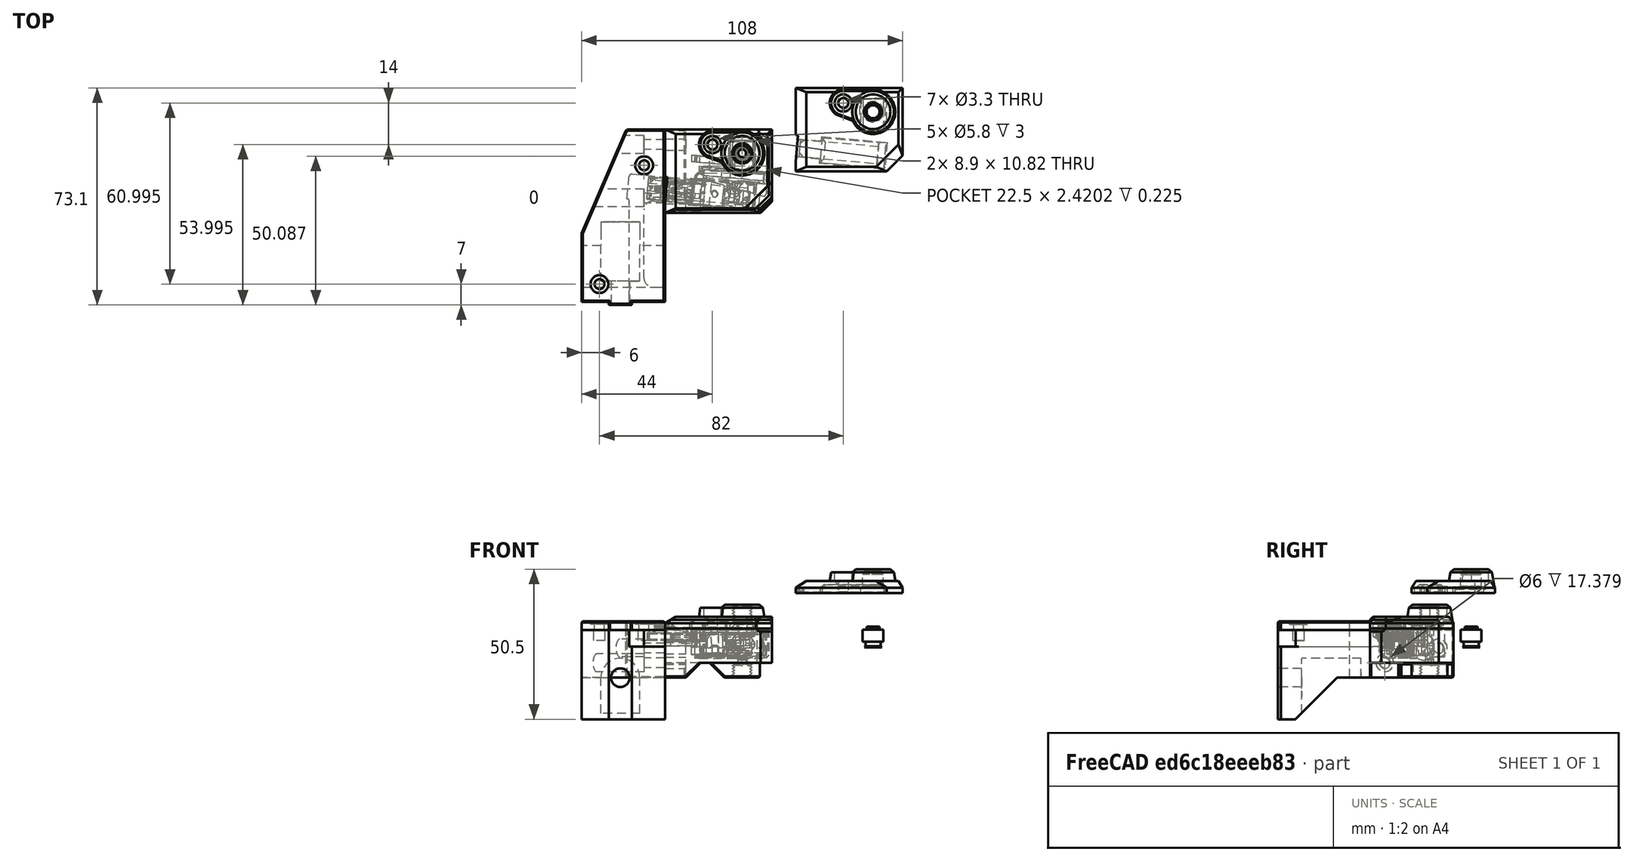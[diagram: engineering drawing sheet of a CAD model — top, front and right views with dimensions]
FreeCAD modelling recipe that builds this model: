
FCSTD DOCUMENT  (FreeCAD 0.18R16146 (Git))
Label: filament-sensor
License: All rights reserved
LicenseURL: http://en.wikipedia.org/wiki/All_rights_reserved
objects: Part::Feature×16, Part::Cylinder×16, Part::MultiFuse×14, Part::Cut×13, Part::Box×10, Part::Chamfer×10, Part::Fillet×3, Part::Extrusion×1
note: 83 computed .brp shape members not serialized (recipe doc carries the construction recipe); baked Part::Feature solids carry a one-line shape summary decoded from their .brp

FEATURE [Part::Feature] Fusion002011011013001  label="Fusion002011011014"
  Placement = pos=(70,20.04,17) rot=(0.57735,0.57735,0.57735;2.0944rad)
  shape: bbox 36.01 x 28.11 x 18.01 mm, 136 faces (baked)
FEATURE [Part::Cylinder] Cylinder004
  Angle = 360
  AttacherType = Attacher::AttachEngine3D
  Height = 10
  Placement = pos=(60,23,19) rot=(0,0,1;0rad)
  Radius = 2.1
FEATURE [Part::Feature] Part__Feature049001  label="fs_cover v029"
  Placement = pos=(57,-160.23,5.5) rot=(0,0,1;1.5708rad)
  shape: bbox 36 x 28.1 x 8 mm, 236 faces (baked)
FEATURE [Part::Box] Box013  label="Cube013"
  AttacherType = Attacher::AttachEngine3D
  Height = 0.5
  Length = 21
  Placement = pos=(48.1,1.8,32) rot=(0,0,1;0rad)
  Width = 12
FEATURE [Part::MultiFuse] Fusion002011011013004002003
  Shapes = -> [Part__Feature049001,Box013]
FEATURE [Part::Feature] Cut023001  label="cap-r1"
  Placement = pos=(-44,-14,-12) rot=(0,0,1;0rad)
  shape: bbox 36 x 28.1 x 8.302 mm, 86 faces (baked)
FEATURE [Part::Feature] Cut004006001001  label="collet-slot"
  Placement = pos=(70.02,20.04,17.14) rot=(0,1,0;3.14159rad)
  shape: bbox 7 x 7 x 7 mm, 9 faces (baked)
FEATURE [Part::Cut] Cut008004003004014002002005003004003002003021008
  Base = -> Fusion002011011013001
  Tool = -> Cylinder004
FEATURE [Part::Feature] Cut008004003004014002002005003004003002003021009  label="collet-slot001"
  Placement = pos=(70.02,20.04,17.14) rot=(0,1,0;3.14159rad)
  shape: bbox 7 x 7 x 7 mm, 9 faces (baked)
FEATURE [Part::Feature] Cut008004003004014002002005003004003002003021011  label="collet-slot002"
  Placement = pos=(70.02,20.04,29.74) rot=(0,0,1;0rad)
  shape: bbox 7 x 7 x 7 mm, 9 faces (baked)
FEATURE [Part::Cut] Cut008004003004014002002005003004003002003021012  label="cap-collet"
  Base = -> Fusion002011011013004002003
  Tool = -> Cut008004003004014002002005003004003002003021011
FEATURE [Part::Cylinder] Cylinder005
  Angle = 360
  AttacherType = Attacher::AttachEngine3D
  Height = 10
  Placement = pos=(70,20.04,11) rot=(0,0,-1;1.5708rad)
  Radius = 1.3
FEATURE [Part::Cut] Cut008004003004014002002005003004003002003021013
  Base = -> Cut008004003004014002002005003004003002003021008
  Tool = -> Cylinder005
FEATURE [Part::Feature] Cut022  label="thread"
  Placement = pos=(70,20,10.4) rot=(0,0,1;0rad)
  shape: bbox 6.8 x 6.8 x 5.777 mm, 9 faces (baked)
FEATURE [Part::Cut] Cut008004003004014002002005003004003002003021014
  Base = -> Cut008004003004014002002005003004003002003021013
  Placement = pos=(-44,-14,-17) rot=(0,0,1;0rad)
  Tool = -> Cut022
FEATURE [Part::Cylinder] Cylinder
  Angle = 360
  AttacherType = Attacher::AttachEngine3D
  Height = 7
  Placement = pos=(-1.1e-15,9,5) rot=(0,1,0;1.5708rad)
  Radius = 1.9
FEATURE [Part::Cylinder] Cylinder006
  Angle = 360
  AttacherType = Attacher::AttachEngine3D
  Height = 7
  Placement = pos=(0,-9,0) rot=(0,1,0;1.5708rad)
  Radius = 1.9
FEATURE [Part::Box] Box  label="Cube"
  AttacherType = Attacher::AttachEngine3D
  Height = 6
  Length = 12
  Placement = pos=(0,-14,-5) rot=(0,0,1;0rad)
  Width = 10
FEATURE [Part::Chamfer] Chamfer
  Base = -> Box
  Edges = 1 edges r=5: [Edge8]
FEATURE [Part::Chamfer] Chamfer001
  Base = -> Chamfer
  Edges = 4 edges r=0.4: [Edge5,Edge6,Edge10,Edge13]
FEATURE [Part::MultiFuse] Fusion
  Shapes = -> [Cut008004003004014002002005003004003002003021014,Chamfer001]
FEATURE [Part::MultiFuse] Fusion002011011013004002004
  Shapes = -> [Cylinder,Cylinder006]
FEATURE [Part::Cut] Cut
  Base = -> Fusion
  Placement = pos=(0,0,5) rot=(0,0,1;0rad)
  Tool = -> Fusion002011011013004002004
FEATURE [Part::Box] Box014  label="Cube014"
  AttacherType = Attacher::AttachEngine3D
  Height = 16
  Length = 28
  Placement = pos=(-28,-44,0) rot=(0,0,1;0rad)
  Width = 58.1
FEATURE [Part::Box] Box015  label="Cube015"
  AttacherType = Attacher::AttachEngine3D
  Height = 4.9
  Length = 8
  Placement = pos=(-1,-3.9,0) rot=(0,0,1;0rad)
  Width = 18
FEATURE [Part::Chamfer] Chamfer003
  Base = -> Cut
  Edges = 1 edges r=5: [Edge68]
FEATURE [Part::Feature] Defeatured
  shape: bbox 36 x 28.1 x 8.302 mm, 85 faces (baked)
FEATURE [Part::Feature] Defeatured001
  shape: bbox 36 x 28.1 x 8.302 mm, 84 faces (baked)
FEATURE [Part::Feature] Defeatured002
  shape: bbox 36 x 28.1 x 8.302 mm, 83 faces (baked)
FEATURE [Part::Chamfer] Chamfer004
  Base = -> Defeatured002
  Edges = 1 edges r=5: [Edge55]
FEATURE [Part::Chamfer] Chamfer005
  Base = -> Chamfer004
  Edges = 4 edges r=1: [Edge28,Edge33,Edge36,Edge45]
FEATURE [Part::Chamfer] Chamfer006
  Base = -> Box015
  Edges = 12 edges r=0.4: [Edge1,Edge2,Edge3,Edge4,Edge5,Edge6,Edge7,Edge8,Edge9,Edge10,Edge11,Edge12]
FEATURE [Part::Box] Box016  label="Cube016"
  AttacherType = Attacher::AttachEngine3D
  Height = 16
  Length = 28
  Placement = pos=(-28,-44,-14) rot=(0,0,1;0rad)
  Width = 5
FEATURE [Part::Cylinder] Cylinder007
  Angle = 360
  AttacherType = Attacher::AttachEngine3D
  Height = 43
  Placement = pos=(-2.2e-15,9,10) rot=(0,1,0;4.71239rad)
  Radius = 1.65
FEATURE [Part::Cylinder] Cylinder008
  Angle = 360
  AttacherType = Attacher::AttachEngine3D
  Height = 43
  Placement = pos=(-3.1e-15,-9,5) rot=(0,-1,0;1.5708rad)
  Radius = 1.65
FEATURE [Part::Cylinder] Cylinder009
  Angle = 360
  AttacherType = Attacher::AttachEngine3D
  Height = 43
  Placement = pos=(-2e-15,9,10) rot=(0,-1,0;1.5708rad)
  Radius = 3
FEATURE [Part::Cylinder] Cylinder010
  Angle = 360
  AttacherType = Attacher::AttachEngine3D
  Height = 43
  Placement = pos=(-3.1e-15,-9,5) rot=(0,-1,0;1.5708rad)
  Radius = 3
FEATURE [Part::MultiFuse] Fusion002011011013004002006
  Shapes = -> [Cylinder007,Cylinder008]
FEATURE [Part::MultiFuse] Fusion002011011013004002007
  Placement = pos=(-7,0,0) rot=(0,0,1;0rad)
  Shapes = -> [Cylinder010,Cylinder009]
FEATURE [Part::MultiFuse] Fusion002011011013004002008
  Shapes = -> [Fusion002011011013004002007,Fusion002011011013004002006]
FEATURE [Part::Box] Box017  label="Cube017"
  AttacherType = Attacher::AttachEngine3D
  Height = 30
  Length = 7.8
  Placement = pos=(-18.9,-45,-14) rot=(0,0,1;0rad)
  Width = 2
FEATURE [Part::Cylinder] Cylinder011
  Angle = 360
  AttacherType = Attacher::AttachEngine3D
  Height = 20
  Placement = pos=(-15,-17,3.8e-15) rot=(1,0,0;1.5708rad)
  Radius = 6.5
FEATURE [Part::Cylinder] Cylinder012
  Angle = 360
  AttacherType = Attacher::AttachEngine3D
  Height = 35
  Placement = pos=(-15,-17,3.8e-15) rot=(1,0,0;1.5708rad)
  Radius = 3.15
FEATURE [Part::MultiFuse] Fusion002011011013004002009
  Shapes = -> [Box014,Box016]
FEATURE [Part::Chamfer] Chamfer007
  Base = -> Fusion002011011013004002009
  Edges = 1 edges r=13.99: [Edge27]
FEATURE [Part::MultiFuse] Fusion002011011013004002010
  Shapes = -> [Chamfer007,Box017]
FEATURE [Part::MultiFuse] Fusion002011011013004002011
  Shapes = -> [Cylinder011,Cylinder012]
FEATURE [Part::Cut] Cut008004003004014002002005003004003002003021015
  Base = -> Fusion002011011013004002010
  Tool = -> Fusion002011011013004002011
FEATURE [Part::Chamfer] Chamfer008
  Base = -> Cut008004003004014002002005003004003002003021015
  Edges = 1 edges: [Edge34 r1=35 r2=15]
FEATURE [Part::Chamfer] Chamfer009
  Base = -> Chamfer008
  Edges = 2 edges r=0.4: [Edge10,Edge11]
FEATURE [Part::Cut] Cut008004003004014002002005003004003002003021016
  Base = -> Chamfer009
  Tool = -> Fusion002011011013004002008
FEATURE [Part::MultiFuse] Fusion002011011013004002012
  Shapes = -> [Cut008004003004014002002005003004003002003021016,Chamfer006]
FEATURE [Part::Box] Box018  label="Cube018"
  AttacherType = Attacher::AttachEngine3D
  Height = 14
  Length = 13
  Placement = pos=(-21.5,-37,-14) rot=(0,0,1;0rad)
  Width = 17
FEATURE [Part::Cut] Cut008004003004014002002005003004003002003021017
  Base = -> Fusion002011011013004002012
  Tool = -> Box018
FEATURE [Part::Feature] Cut008004003004014002002005003004003002003021017_cs
  Placement = pos=(0,0,19.5) rot=(0,0,1;0rad)
  shape: bbox 28 x 59.1 x 3e-07 mm, 0 faces, 0 solids (baked)
FEATURE [Part::Box] Box019  label="Cube019"
  AttacherType = Attacher::AttachEngine3D
  Height = 10
  Length = 14
  Placement = pos=(-12.7147,-9.24194,10.5) rot=(0,0,1;6.19592rad)
  Width = 8.4
FEATURE [Part::Cut] Cut008004003004014002002005003004003002003021018
  Base = -> Cut008004003004014002002005003004003002003021017
  Tool = -> Box019
FEATURE [Part::Box] Box020  label="Cube020"
  AttacherType = Attacher::AttachEngine3D
  Height = 10
  Length = 13
  Placement = pos=(-12,-46,10.5) rot=(0,0,1;0rad)
  Width = 7
FEATURE [Part::Box] Box021  label="Cube021"
  AttacherType = Attacher::AttachEngine3D
  Height = 10
  Length = 5
  Placement = pos=(-12,-44,10.5) rot=(0,0,1;0rad)
  Width = 39
FEATURE [Part::MultiFuse] Fusion002011011013004002013
  Shapes = -> [Box020,Box021]
FEATURE [Part::Cut] Cut008004003004014002002005003004003002003021019
  Base = -> Cut008004003004014002002005003004003002003021018
  Tool = -> Fusion002011011013004002013
FEATURE [Part::Fillet] Fillet
  Base = -> Cut008004003004014002002005003004003002003021019
  Edges = 2 edges r=3: [Edge76,Edge80]
FEATURE [Part::Fillet] Fillet001
  Base = -> Fillet
  Edges = 2 edges r=1: [Edge7,Edge59]
FEATURE [Part::Fillet] Fillet002
  Base = -> Fillet001
  Edges = 1 edges r=0.7: [Edge59]
FEATURE [Part::Extrusion] Extrude
  Base = -> Cut008004003004014002002005003004003002003021017_cs
  Dir = (0,0,1)
  DirMode = 2
  FaceMakerClass = Part::FaceMakerBullseye
  LengthFwd = 3
  LengthRev = 0
  Placement = pos=(0,0,-18.5) rot=(0,0,1;0rad)
  Solid = true
  Symmetric = false
FEATURE [Part::Chamfer] Chamfer010
  Base = -> Extrude
  Edges = 12 edges r=0.4: [Edge4,Edge7,Edge10,Edge13,Edge16,Edge17,Edge19,Edge20,Edge22,Edge25,Edge28,Edge30]
FEATURE [Part::Cylinder] Cylinder013
  Angle = 360
  AttacherType = Attacher::AttachEngine3D
  Height = 10
  Placement = pos=(-7,2,12.5) rot=(0,0,1;0rad)
  Radius = 1.65
FEATURE [Part::Cylinder] Cylinder014
  Angle = 360
  AttacherType = Attacher::AttachEngine3D
  Height = 10
  Placement = pos=(-22,-38,12.5) rot=(0,0,1;0rad)
  Radius = 1.65
FEATURE [Part::Cylinder] Cylinder015
  Angle = 360
  AttacherType = Attacher::AttachEngine3D
  Height = 10
  Placement = pos=(-22,-38,12.5) rot=(0,0,1;0rad)
  Radius = 1.9
FEATURE [Part::Cylinder] Cylinder016
  Angle = 360
  AttacherType = Attacher::AttachEngine3D
  Height = 10
  Placement = pos=(-7,2,12.5) rot=(0,0,1;0rad)
  Radius = 1.9
FEATURE [Part::MultiFuse] Fusion002011011013004002014
  Shapes = -> [Cylinder016,Cylinder015]
FEATURE [Part::Cut] Cut008004003004014002002005003004003002003021020
  Base = -> Fillet002
  Tool = -> Fusion002011011013004002014
FEATURE [Part::MultiFuse] Fusion002011011013004002015
  Shapes = -> [Cylinder013,Cylinder014]
FEATURE [Part::Cylinder] Cylinder017
  Angle = 360
  AttacherType = Attacher::AttachEngine3D
  Height = 10
  Placement = pos=(-22,-38,12.5) rot=(0,0,1;0rad)
  Radius = 3
FEATURE [Part::Cylinder] Cylinder018
  Angle = 360
  AttacherType = Attacher::AttachEngine3D
  Height = 10
  Placement = pos=(-7,2,12.5) rot=(0,0,1;0rad)
  Radius = 3
FEATURE [Part::Cut] Cut008004003004014002002005003004003002003021021
  Base = -> Chamfer010
  Tool = -> Fusion002011011013004002015
FEATURE [Part::MultiFuse] Fusion002011011013004002016
  Placement = pos=(0,0,5.5) rot=(0,0,1;0rad)
  Shapes = -> [Cylinder017,Cylinder018]
FEATURE [Part::Cut] Cut008004003004014002002005003004003002003021022
  Base = -> Cut008004003004014002002005003004003002003021021
  Tool = -> Fusion002011011013004002016
FEATURE [Part::Feature] Part__Feature032  label="fs_lever"
  Placement = pos=(9.025,1.8,-14.7) rot=(0.57735,0.57735,0.57735;2.0944rad)
  shape: bbox 24.12 x 9.285 x 8.809 mm, 52 faces (baked)
FEATURE [Part::Feature] Part__Feature043  label="magnet_20x6x2 v1"
  Placement = pos=(13.2434,0.574978,10.1) rot=(-0.998099,0.043578,0.043578;4.71049rad)
  shape: bbox 20.1 x 3.736 x 6 mm, 6 faces (baked)
FEATURE [Part::Feature] Part__Feature044  label="magnet_10x6x2 v1"
  Placement = pos=(20.7471,4.30646,16.4) rot=(0.030858,0.70677,-0.70677;3.20329rad)
  shape: bbox 10.14 x 2.864 x 6 mm, 6 faces (baked)
FEATURE [Part::Feature] Part__Feature045  label="steel_ball v1"
  Placement = pos=(25.9855,4.08709,9.4) rot=(0.999969,0.005607,-0.005607;4.71236rad)
  shape: bbox 7 x 7 x 7 mm, 1 faces (baked)
FEATURE [Part::Feature] Fusion001
  Placement = pos=(14,-174.2,-6.7) rot=(0,0,1;1.5708rad)
  shape: bbox 36.02 x 10.86 x 8.121 mm, 301 faces (baked)
